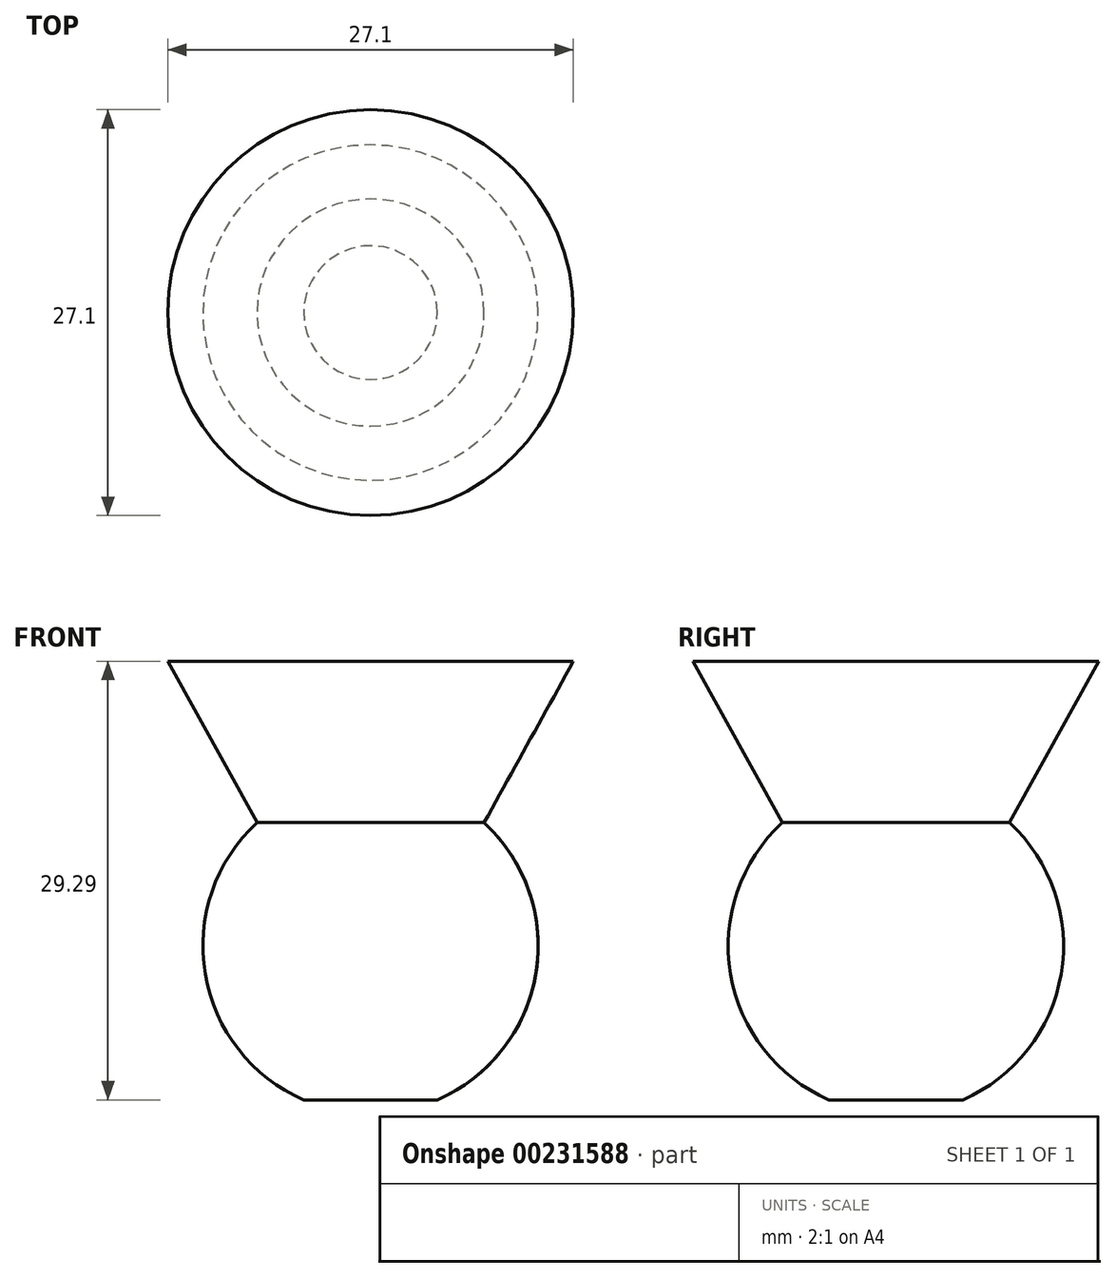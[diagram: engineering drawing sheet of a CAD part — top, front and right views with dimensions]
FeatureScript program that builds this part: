
annotation { "Feature Type Name" : "Feature", "Feature Type Description" : "" }
export const myFeature = defineFeature(function(context is Context, id is Id, definition is map)
    precondition{}
    {
        {
            var Q0;
            Q0=qCreatedBy(makeId("Front.planeOp"),FACE);
            var sketch = newSketch(context, id + "F0", { "sketchPlane" : qUnion([Q0])});
            skArc(sketch, "E0", {"start": v(-36.29, 9.18) * mm, "mid": v(-34.2, 3.68) * mm, "end": v(-29.6, 0) * mm});
            skArc(sketch, "E1", {"start": v(-36.29, 9.18) * mm, "mid": v(-35.6, 14.27) * mm, "end": v(-32.72, 18.52) * mm});
            skLineSegment(sketch, "E2", {"start": v(-32.72, 18.52) * mm, "end": v(-38.7, 29.3) * mm});
            skLineSegment(sketch, "E3", {"start": v(-38.7, 29.3) * mm, "end": v(-25.14, 29.3) * mm});
            skLineSegment(sketch, "E4", {"start": v(-25.14, 29.3) * mm, "end": v(-25.14, 10.27) * mm});
            skLineSegment(sketch, "E5", {"start": v(-25.14, 10.27) * mm, "end": v(-25.14, 0) * mm});
            skLineSegment(sketch, "E6", {"start": v(-25.14, 0) * mm, "end": v(-29.6, 0) * mm});
            skLineSegment(sketch, "E7", {"start": v(-25.14, 10.27) * mm, "end": v(-25.14, -32.14) * mm});
            skSolve(sketch);
        }
        {
            var Q0;
            Q0=makeQuery(id+"F0.imprint","IMPRINT",FACE,{"disambiguationData":[TD([[makeQuery(id+"F0.imprint","IMPRINT",EDGE,{"derivedFrom":sQuery(id+"F0.wireOp",EDGE,"E0")}),1.0]])]});
            var Q1;
            Q1=sQuery(id+"F0.wireOp",EDGE,"E7");
            revolve(context, id + "F1", {"entities" : qUnion([Q0]), "axis" : qUnion([Q1]), "revolveType" : RevolveType.FULL});
        }
    });
